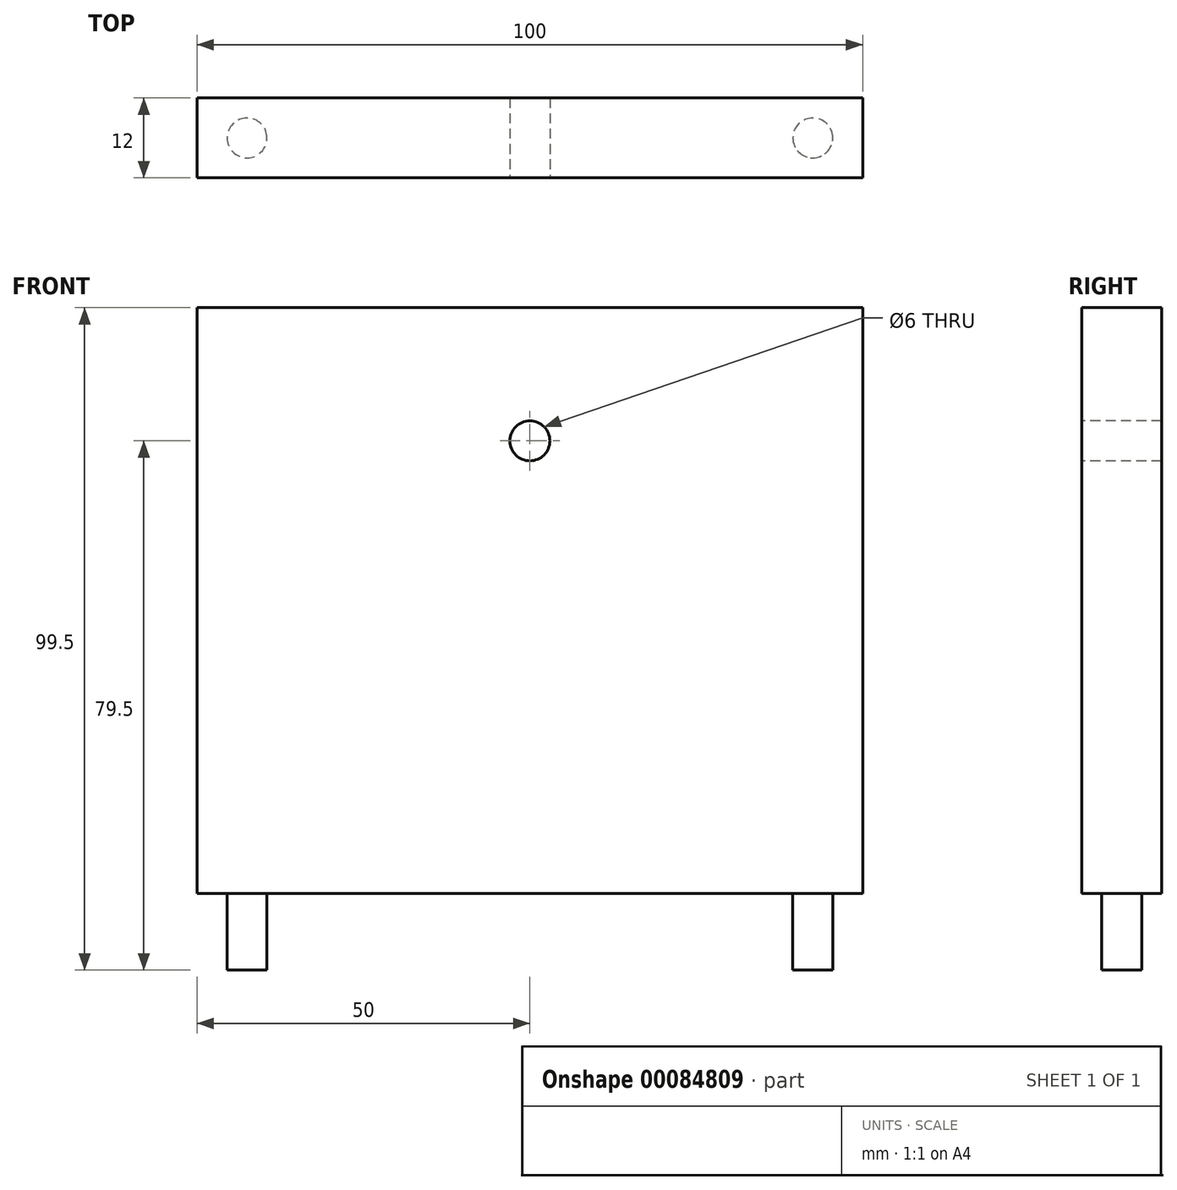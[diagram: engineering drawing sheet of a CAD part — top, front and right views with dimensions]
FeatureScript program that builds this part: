
annotation { "Feature Type Name" : "Feature", "Feature Type Description" : "" }
export const myFeature = defineFeature(function(context is Context, id is Id, definition is map)
    precondition{}
    {
        {
            var Q0;
            Q0=qCreatedBy(makeId("Front.planeOp"),FACE);
            var sketch = newSketch(context, id + "F0", { "sketchPlane" : qUnion([Q0])});
            skLineSegment(sketch, "E0.bottom", {"start": v(0, 0) * mm, "end": v(100, 0) * mm});
            skLineSegment(sketch, "E0.top", {"start": v(0, 88) * mm, "end": v(100, 88) * mm});
            skLineSegment(sketch, "E0.left", {"start": v(0, 0) * mm, "end": v(0, 88) * mm});
            skLineSegment(sketch, "E0.right", {"start": v(100, 0) * mm, "end": v(100, 88) * mm});
            skSolve(sketch);
        }
        {
            var Q0;
            Q0 = qSketchRegion(id + "F0", true);
            extrude(context, id + "F1", {"entities" : qUnion([Q0]), "depth" : 12 * mm});
        }
        {
            var Q0;
            Q0=makeQuery(id+"F1.opExtrude","SWEPT_FACE",FACE,{"disambiguationData":[OSD([sQuery(id+"F0.wireOp",EDGE,"E0.bottom")])]});
            var sketch = newSketch(context, id + "F2", { "sketchPlane" : qUnion([Q0])});
            skLineSegment(sketch, "E1", {"start": v(0, 6) * mm, "end": v(100, 6) * mm, "construction": true});
            skLineSegment(sketch, "E2", {"start": v(7.5, 6) * mm, "end": v(92.5, 6) * mm, "construction": true});
            skCircle(sketch, "E3", {"center": v(7.5, 6) * mm, "radius": 3 * mm});
            skCircle(sketch, "E4", {"center": v(92.5, 6) * mm, "radius": 3 * mm});
            skLineSegment(sketch, "E5", {"start": v(50, 6) * mm, "end": v(50, 29.83) * mm, "construction": true});
            skLineSegment(sketch, "E6", {"start": v(50, 0) * mm, "end": v(50, 12) * mm, "construction": true});
            skSolve(sketch);
        }
        {
            var Q0;
            Q0 = qSketchRegion(id + "F2", true);
            extrude(context, id + "F3", {"entities" : qUnion([Q0]), "operationType" : NewBodyOperationType.ADD, "depth" : 11.5 * mm});
        }
        {
            var Q0;
            Q0=makeQuery(id+"F1.opExtrude","CAP_FACE",FACE,{"disambiguationData":[OSD([sQuery(id+"F0.wireOp",EDGE,"E0.bottom"),sQuery(id+"F0.wireOp",EDGE,"E0.top"),sQuery(id+"F0.wireOp",EDGE,"E0.left"),sQuery(id+"F0.wireOp",EDGE,"E0.right")])],"isStart":false});
            var sketch = newSketch(context, id + "F4", { "sketchPlane" : qUnion([Q0])});
            skLineSegment(sketch, "E7", {"start": v(50, 0) * mm, "end": v(50, 88) * mm, "construction": true});
            skCircle(sketch, "E8", {"center": v(50, 68) * mm, "radius": 3 * mm});
            skSolve(sketch);
        }
        {
            var Q0;
            Q0 = qSketchRegion(id + "F4", true);
            extrude(context, id + "F5", {"entities" : qUnion([Q0]), "operationType" : NewBodyOperationType.REMOVE, "endBound" : BoundingType.THROUGH_ALL, "oppositeDirection" : true, "depth" : 25 * mm});
        }
    });
